# Revit family: Lixeira Sassari 45 L
name_source: partatom
category: Modelos genéricos
units: mm (PartAtom-declared; Revit-internal decimal feet)

## family parameters
Compartilhado = Sim
Corte com vazios quando carregada = Não
Cota do conector redondo = Utilizar diâmetro
Pode hospedar o vergalhão = Não
Ponto de cálculo do ambiente = Não
Sempre na vertical = Não
Tipo de parte = Não definido

## types (1)
- Lixeira Sassari 45 L
    Acabamento = Scotch brite
    Aramado interno para fixação do saco de lixo = Sim
    Balde Plástico = Não
    Descrição = Lixeira Sassari 45L
    Elevação padrão = 0 mm  [stored 0 ft]
    Espessura = 0,6 mm
    Fabricante = Tramontina
    Material (Corpo) = Aço Inox AISI 430
    Material (Estrutura) = Aço carbono com pintura eletrostática a pó preto fosco
    Pegador/Alça para transporte = Sim
    Referência = 94539/445
    Site = https://global.tramontina.com
    Tratamento Antidigitais = Não

note: [stored X ft] marks values corroborated as IEEE doubles in the binary element streams (Revit-internal decimal feet)
